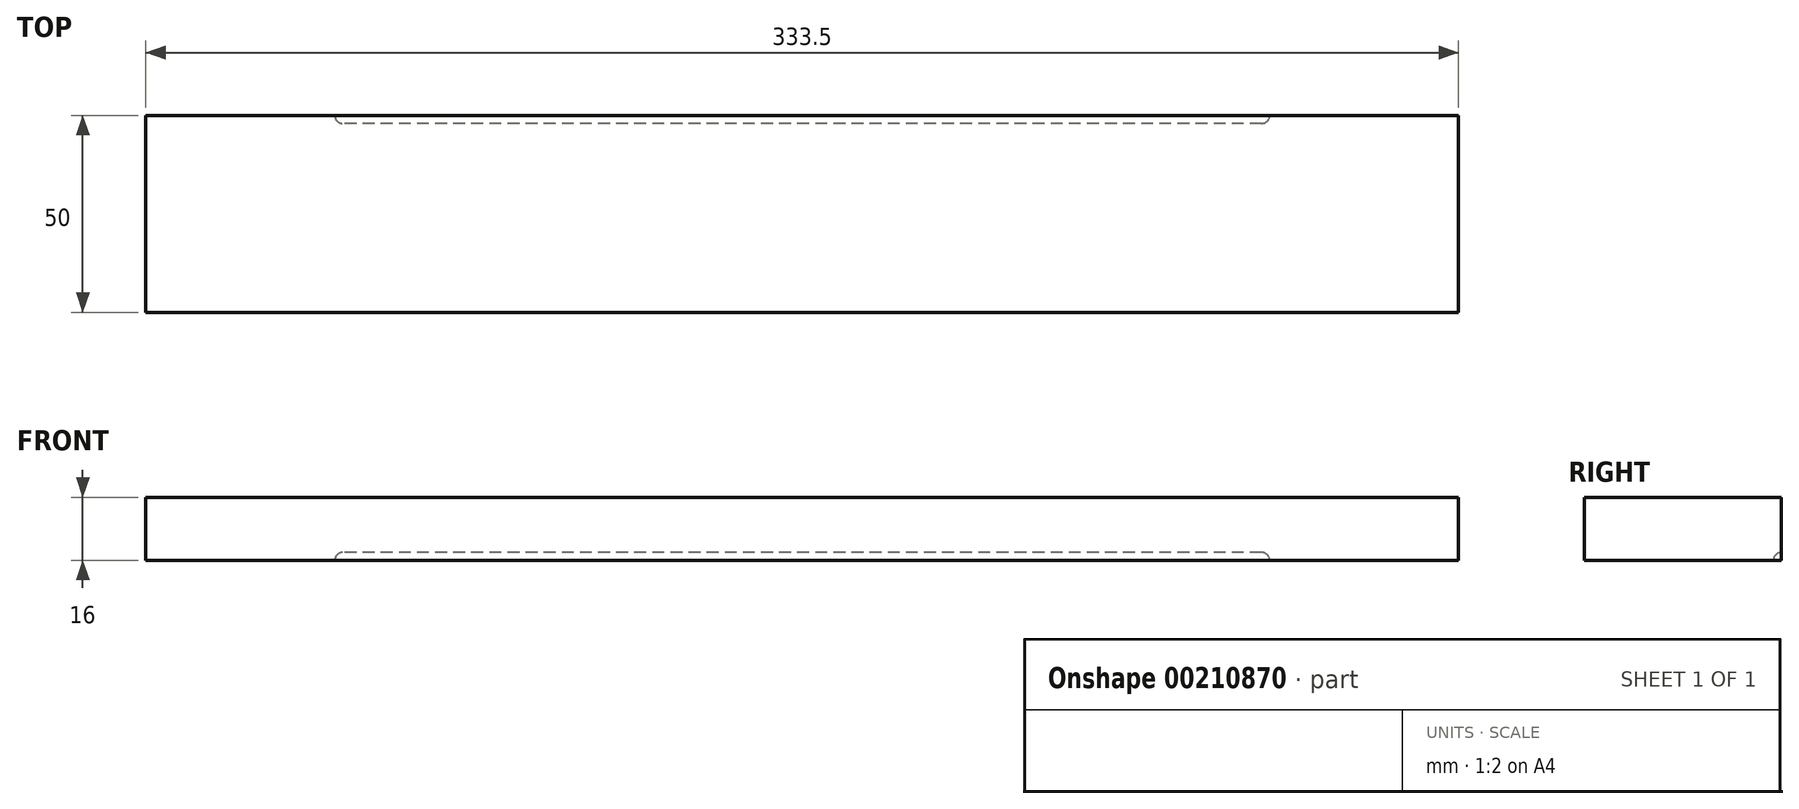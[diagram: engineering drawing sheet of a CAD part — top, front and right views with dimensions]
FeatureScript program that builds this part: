
annotation { "Feature Type Name" : "Feature", "Feature Type Description" : "" }
export const myFeature = defineFeature(function(context is Context, id is Id, definition is map)
    precondition{}
    {
        {
            var Q0;
            Q0=qCreatedBy(makeId("Right.planeOp"),FACE);
            var sketch = newSketch(context, id + "F0", { "sketchPlane" : qUnion([Q0])});
            skLineSegment(sketch, "E0.bottom", {"start": v(25, 8) * mm, "end": v(-25, 8) * mm});
            skLineSegment(sketch, "E0.top", {"start": v(23, -8) * mm, "end": v(-25, -8) * mm});
            skLineSegment(sketch, "E0.left", {"start": v(25, 8) * mm, "end": v(25, -6) * mm});
            skLineSegment(sketch, "E0.right", {"start": v(-25, 8) * mm, "end": v(-25, -8) * mm});
            skPoint(sketch, "E0.middle", {"position": v(0, 0) * mm});
            skArc(sketch, "E1", {"start": v(25, -6) * mm, "mid": v(23.59, -6.59) * mm, "end": v(23, -8) * mm});
            skSolve(sketch);
        }
        {
            var Q0;
            Q0 = qSketchRegion(id + "F0", true);
            extrude(context, id + "F1", {"entities" : qUnion([Q0]), "endBound" : BoundingType.SYMMETRIC, "depth" : 333.5 * mm});
        }
        {
            var Q0;
            Q0=makeQuery(id+"F1.opExtrude","SWEPT_FACE",FACE,{"disambiguationData":[OSD([sQuery(id+"F0.wireOp",EDGE,"E0.left")])]});
            var sketch = newSketch(context, id + "F2", { "sketchPlane" : qUnion([Q0])});
            skLineSegment(sketch, "E2.bottom", {"start": v(-166.75, 8) * mm, "end": v(-116.75, 8) * mm});
            skLineSegment(sketch, "E2.top", {"start": v(-166.75, -8) * mm, "end": v(-116.75, -8) * mm});
            skLineSegment(sketch, "E2.left", {"start": v(-166.75, 8) * mm, "end": v(-166.75, -8) * mm});
            skLineSegment(sketch, "E2.right", {"start": v(-116.75, 8) * mm, "end": v(-116.75, -8) * mm});
            skSolve(sketch);
        }
        {
            var Q0;
            Q0 = qSketchRegion(id + "F2", true);
            extrude(context, id + "F3", {"entities" : qUnion([Q0]), "operationType" : NewBodyOperationType.ADD, "oppositeDirection" : true, "depth" : 2 * mm});
        }
        {
            var Q0;
            Q0=makeQuery(id+"F3.boolean.opBoolean","MERGE",FACE,{"derivedFrom":[makeQuery(id+"F1.opExtrude","SWEPT_FACE",FACE,{"disambiguationData":[OSD([sQuery(id+"F0.wireOp",EDGE,"E0.left")])]}),makeQuery(id+"F3.opExtrude","CAP_FACE",FACE,{"disambiguationData":[OSD([sQuery(id+"F2.wireOp",EDGE,"E2.bottom"),sQuery(id+"F2.wireOp",EDGE,"E2.top"),sQuery(id+"F2.wireOp",EDGE,"E2.left"),sQuery(id+"F2.wireOp",EDGE,"E2.right")])],"isStart":true})]});
            var sketch = newSketch(context, id + "F4", { "sketchPlane" : qUnion([Q0])});
            skLineSegment(sketch, "E3.bottom", {"start": v(166.75, 8) * mm, "end": v(116.75, 8) * mm});
            skLineSegment(sketch, "E3.top", {"start": v(166.75, -8) * mm, "end": v(116.75, -8) * mm});
            skLineSegment(sketch, "E3.left", {"start": v(166.75, 8) * mm, "end": v(166.75, -8) * mm});
            skLineSegment(sketch, "E3.right", {"start": v(116.75, 8) * mm, "end": v(116.75, -8) * mm});
            skSolve(sketch);
        }
        {
            var Q0;
            Q0 = qSketchRegion(id + "F4", true);
            extrude(context, id + "F5", {"entities" : qUnion([Q0]), "operationType" : NewBodyOperationType.ADD, "oppositeDirection" : true, "depth" : 2 * mm});
        }
        {
            var Q0;
            Q0=makeQuery(id+"F5.boolean.opBoolean","MERGE",FACE,{"derivedFrom":[makeQuery(id+"F3.boolean.opBoolean","MERGE",FACE,{"derivedFrom":[makeQuery(id+"F1.opExtrude","SWEPT_FACE",FACE,{"disambiguationData":[OSD([sQuery(id+"F0.wireOp",EDGE,"E0.top")])]}),makeQuery(id+"F3.opExtrude","SWEPT_FACE",FACE,{"disambiguationData":[OSD([sQuery(id+"F2.wireOp",EDGE,"E2.top")])]})]}),makeQuery(id+"F5.opExtrude","SWEPT_FACE",FACE,{"disambiguationData":[OSD([sQuery(id+"F4.wireOp",EDGE,"E3.top")])]})]});
            var sketch = newSketch(context, id + "F6", { "sketchPlane" : qUnion([Q0])});
            skPoint(sketch, "E4.end.orphan", {"position": v(-116.75, -23) * mm});
            skPoint(sketch, "E4.start.orphan", {"position": v(-116.75, -25) * mm});
            skArc(sketch, "E5", {"start": v(-116.75, -23) * mm, "mid": v(-118.16, -23.59) * mm, "end": v(-118.75, -25) * mm});
            skLineSegment(sketch, "E6", {"start": v(-118.75, -25) * mm, "end": v(-116.75, -25) * mm});
            skLineSegment(sketch, "E7", {"start": v(-116.75, -23) * mm, "end": v(-116.75, -25) * mm});
            skCircle(sketch, "E8", {"center": v(116.75, -25) * mm, "radius": 2 * mm});
            skLineSegment(sketch, "E9", {"start": v(116.75, -23) * mm, "end": v(116.75, -27) * mm});
            skSolve(sketch);
        }
        {
            var Q0;
            {var subQ0=sQuery(id+"F6.wireOp",EDGE,"E9");var subQ4=makeQuery(id+"F6.imprint","INTERSECT",VERTEX,{"derivedFrom":[makeQuery(id+"F3.opExtrude","CAP_EDGE",EDGE,{"disambiguationData":[OSD([sQuery(id+"F2.wireOp",EDGE,"E2.top")])],"isStart":true}),subQ0]});Q0=makeQuery(id+"F6.imprint","IMPRINT",FACE,{"disambiguationData":[TD([[makeQuery(id+"F6.imprint","IMPRINT",EDGE,{"disambiguationData":[TD([[subQ4,-1.0]])],"derivedFrom":subQ0}),-1.0]])]});}
            var Q1;
            Q1=sQuery(id+"F6.wireOp",EDGE,"E9");
            var Q2;
            Q2=sQuery(id+"F6.wireOp",EDGE,"E9");
            revolve(context, id + "F7", {"operationType" : NewBodyOperationType.REMOVE, "entities" : qUnion([Q0]), "surfaceEntities" : qUnion([Q1]), "axis" : qUnion([Q2]), "revolveType" : RevolveType.FULL, "oppositeDirection" : true});
        }
        {
            var Q0;
            Q0=makeQuery(id+"F5.boolean.opBoolean","MERGE",FACE,{"derivedFrom":[makeQuery(id+"F3.boolean.opBoolean","MERGE",FACE,{"derivedFrom":[makeQuery(id+"F1.opExtrude","SWEPT_FACE",FACE,{"disambiguationData":[OSD([sQuery(id+"F0.wireOp",EDGE,"E0.left")])]}),makeQuery(id+"F3.opExtrude","CAP_FACE",FACE,{"disambiguationData":[OSD([sQuery(id+"F2.wireOp",EDGE,"E2.bottom"),sQuery(id+"F2.wireOp",EDGE,"E2.top"),sQuery(id+"F2.wireOp",EDGE,"E2.left"),sQuery(id+"F2.wireOp",EDGE,"E2.right")])],"isStart":true})]}),makeQuery(id+"F5.opExtrude","CAP_FACE",FACE,{"disambiguationData":[OSD([sQuery(id+"F4.wireOp",EDGE,"E3.bottom"),sQuery(id+"F4.wireOp",EDGE,"E3.top"),sQuery(id+"F4.wireOp",EDGE,"E3.left"),sQuery(id+"F4.wireOp",EDGE,"E3.right")])],"isStart":true})]});
            var sketch = newSketch(context, id + "F8", { "sketchPlane" : qUnion([Q0])});
            skCircle(sketch, "E10", {"center": v(116.75, -8) * mm, "radius": 2 * mm});
            skLineSegment(sketch, "E11", {"start": v(116.75, -6) * mm, "end": v(116.75, -10) * mm});
            skSolve(sketch);
        }
        {
            var Q0;
            {var subQ0=sQuery(id+"F8.wireOp",EDGE,"E11");var subQ4=makeQuery(id+"F8.imprint","INTERSECT",VERTEX,{"derivedFrom":[makeQuery(id+"F5.opExtrude","CAP_EDGE",EDGE,{"disambiguationData":[OSD([sQuery(id+"F4.wireOp",EDGE,"E3.top")])],"isStart":true}),subQ0]});Q0=makeQuery(id+"F8.imprint","IMPRINT",FACE,{"disambiguationData":[TD([[makeQuery(id+"F8.imprint","IMPRINT",EDGE,{"disambiguationData":[TD([[subQ4,-1.0]])],"derivedFrom":subQ0}),-1.0]])]});}
            var Q1;
            Q1=sQuery(id+"F8.wireOp",EDGE,"E11");
            var Q2;
            Q2=sQuery(id+"F8.wireOp",EDGE,"E11");
            revolve(context, id + "F9", {"operationType" : NewBodyOperationType.REMOVE, "entities" : qUnion([Q0]), "surfaceEntities" : qUnion([Q1]), "axis" : qUnion([Q2]), "revolveType" : RevolveType.FULL, "oppositeDirection" : true});
        }
    });
